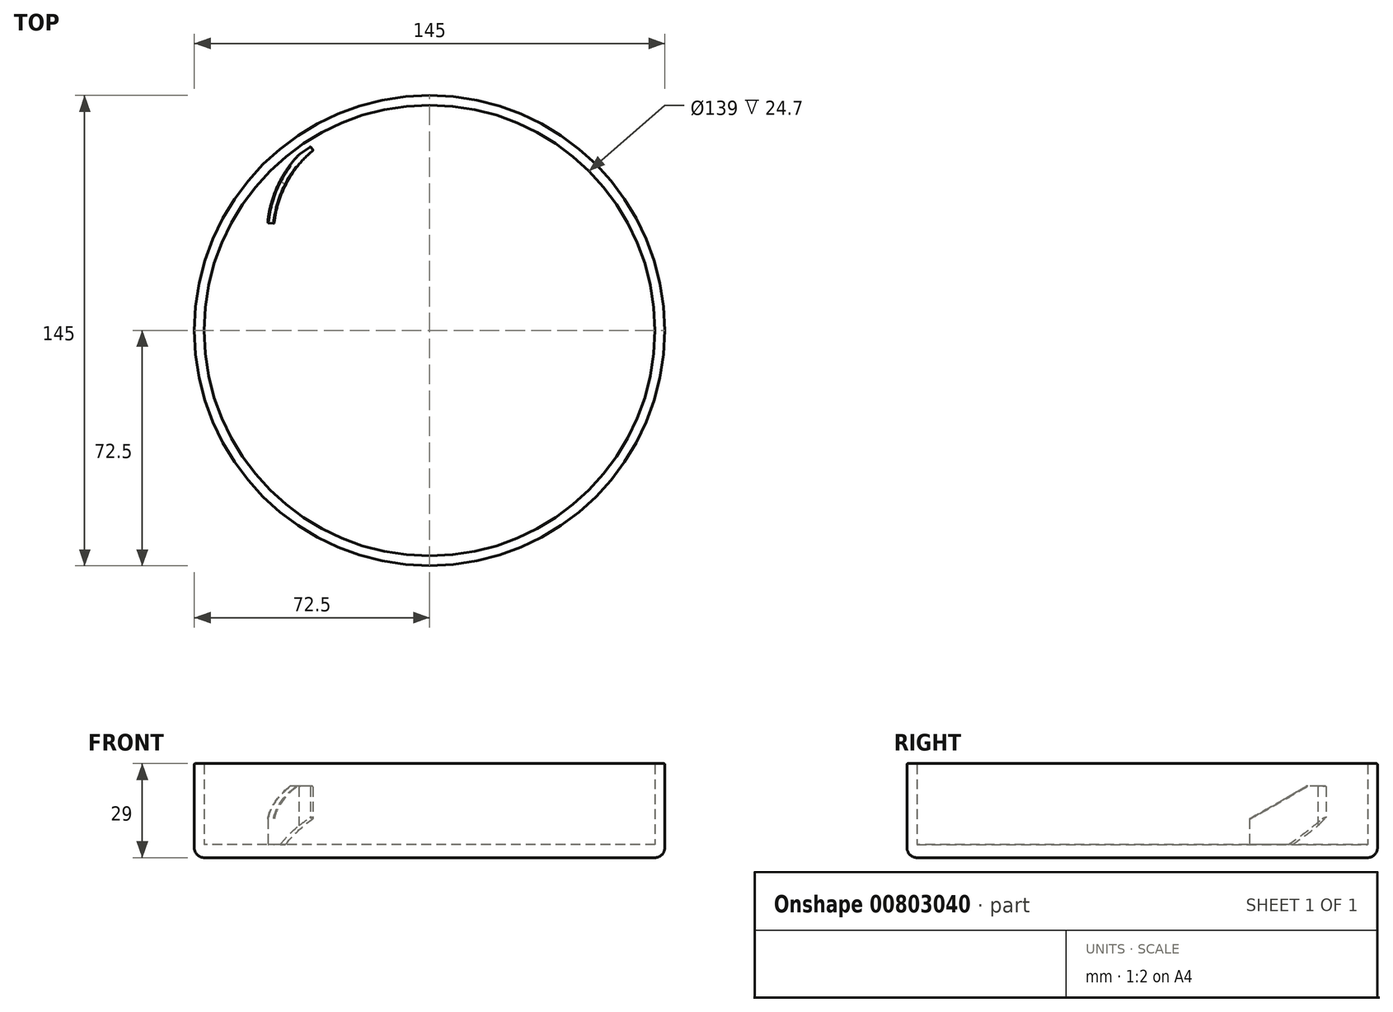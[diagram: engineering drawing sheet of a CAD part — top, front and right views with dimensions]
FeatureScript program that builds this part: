
annotation { "Feature Type Name" : "Feature", "Feature Type Description" : "" }
export const myFeature = defineFeature(function(context is Context, id is Id, definition is map)
    precondition{}
    {
        {
            var Q0;
            Q0=qCreatedBy(makeId("Top.planeOp"),FACE);
            var sketch = newSketch(context, id + "F0", { "sketchPlane" : qUnion([Q0])});
            skCircle(sketch, "E0", {"center": v(0, 0) * mm, "radius": 72.5 * mm});
            skSolve(sketch);
        }
        {
            var Q0;
            Q0 = qSketchRegion(id + "F0", true);
            extrude(context, id + "F1", {"entities" : qUnion([Q0]), "depth" : 4 * mm, "offsetDistance" : 25 * mm});
        }
        {
            var Q0;
            Q0=makeQuery(id+"F1.opExtrude","CAP_FACE",FACE,{"disambiguationData":[OSD([sQuery(id+"F0.wireOp",EDGE,"E0")])],"isStart":false});
            var sketch = newSketch(context, id + "F2", { "sketchPlane" : qUnion([Q0])});
            skCircle(sketch, "E1", {"center": v(0, 0) * mm, "radius": 69.5 * mm});
            skSolve(sketch);
        }
        {
            var Q0;
            Q0=makeQuery(id+"F2.imprint","IMPRINT",FACE,{"disambiguationData":[TD([[makeQuery(id+"F2.imprint","IMPRINT",EDGE,{"derivedFrom":sQuery(id+"F2.wireOp",EDGE,"E1")}),-1.0]])]});
            extrude(context, id + "F3", {"entities" : qUnion([Q0]), "operationType" : NewBodyOperationType.ADD, "depth" : 25 * mm, "offsetDistance" : 25 * mm});
        }
        {
            var Q0;
            Q0=makeQuery(id+"F1.opExtrude","CAP_FACE",FACE,{"disambiguationData":[OSD([sQuery(id+"F0.wireOp",EDGE,"E0")])],"isStart":false});
            var sketch = newSketch(context, id + "F4", { "sketchPlane" : qUnion([Q0])});
            skArc(sketch, "E2", {"start": v(-37.1, 57.14) * mm, "mid": v(-45.9, 46.45) * mm, "end": v(-49.86, 33.18) * mm});
            skArc(sketch, "E3", {"start": v(-35.83, 55.6) * mm, "mid": v(-44.13, 45.51) * mm, "end": v(-47.86, 33) * mm});
            skLineSegment(sketch, "E4", {"start": v(-35.83, 55.6) * mm, "end": v(-37.1, 57.14) * mm});
            skLineSegment(sketch, "E5", {"start": v(-47.86, 33) * mm, "end": v(-49.86, 33.18) * mm});
            skSolve(sketch);
        }
        {
            var Q0;
            Q0 = qSketchRegion(id + "F4", true);
            extrude(context, id + "F5", {"entities" : qUnion([Q0]), "operationType" : NewBodyOperationType.ADD, "depth" : 18 * mm, "offsetDistance" : 25 * mm});
        }
        {
            var Q0;
            Q0=qCreatedBy(makeId("Right.planeOp"),FACE);
            cPlane(context, id + "F6", {"entities" : qUnion([Q0]), "cplaneType" : CPlaneType.OFFSET, "offset" : 35 * mm, "oppositeDirection" : true, "width" : 150 * mm, "height" : 150 * mm});
        }
        {
            var Q0;
            Q0=qCreatedBy(id+"F6.planeOp",FACE);
            var sketch = newSketch(context, id + "F7", { "sketchPlane" : qUnion([Q0])});
            skLineSegment(sketch, "E6", {"start": v(57.14, 4) * mm, "end": v(42.14, 4) * mm});
            skLineSegment(sketch, "E7", {"start": v(42.14, 4) * mm, "end": v(57.14, 13) * mm});
            skLineSegment(sketch, "E8", {"start": v(57.14, 13) * mm, "end": v(57.14, 4) * mm});
            skLineSegment(sketch, "E9", {"start": v(59.14, 4) * mm, "end": v(59.14, 17.57) * mm});
            skSolve(sketch);
        }
        {
            var Q0;
            Q0=makeQuery(id+"F7.imprint","IMPRINT",FACE,{"disambiguationData":[TD([[makeQuery(id+"F7.imprint","IMPRINT",EDGE,{"derivedFrom":sQuery(id+"F7.wireOp",EDGE,"E6")}),-1.0]])]});
            var Q1;
            Q1=sQuery(id+"F7.wireOp",EDGE,"E9");
            revolve(context, id + "F8", {"operationType" : NewBodyOperationType.REMOVE, "surfaceOperationType" : NewSurfaceOperationType.NEW, "entities" : qUnion([Q0]), "axis" : qUnion([Q1]), "revolveType" : RevolveType.ONE_DIRECTION, "oppositeDirection" : true, "angle" : 50 * degree});
        }
        {
            var Q0;
            Q0=makeQuery(id+"F5.opExtrude","CAP_EDGE",EDGE,{"disambiguationData":[OSD([sQuery(id+"F4.wireOp",EDGE,"E5")])],"isStart":false});
            chamfer(context, id + "F9", {"entities" : qUnion([Q0]), "chamferType" : ChamferType.TWO_OFFSETS, "width1" : 10 * mm, "oppositeDirection" : false, "width2" : 18 * mm, "tangentPropagation" : true});
        }
        {
            var Q0;
            Q0=makeQuery(id+"F5.opExtrude","SWEPT_EDGE",EDGE,{"disambiguationData":[OSD([sQuery(id+"F4.wireOp",EDGE,"E3"),sQuery(id+"F4.wireOp",EDGE,"E5")])]});
            var Q1;
            Q1=makeQuery(id+"F5.opExtrude","SWEPT_EDGE",EDGE,{"disambiguationData":[OSD([sQuery(id+"F4.wireOp",EDGE,"E2"),sQuery(id+"F4.wireOp",EDGE,"E5")])]});
            var Q2;
            Q2=makeQuery(id+"F9.opChamfer","BLEND_FACE",FACE,{"disambiguationData":[OSD([sQuery(id+"F4.wireOp",EDGE,"E5")])]});
            var Q3;
            Q3=makeQuery(id+"F5.opExtrude","CAP_FACE",FACE,{"disambiguationData":[OSD([sQuery(id+"F4.wireOp",EDGE,"E2"),sQuery(id+"F4.wireOp",EDGE,"E3"),sQuery(id+"F4.wireOp",EDGE,"E4"),sQuery(id+"F4.wireOp",EDGE,"E5")])],"isStart":false});
            var Q4;
            Q4=makeQuery(id+"F5.opExtrude","SWEPT_EDGE",EDGE,{"disambiguationData":[OSD([sQuery(id+"F4.wireOp",EDGE,"E3"),sQuery(id+"F4.wireOp",EDGE,"E4")])]});
            var Q5;
            Q5=makeQuery(id+"F8.boolean.opBoolean","INTERSECT",EDGE,{"derivedFrom":[makeQuery(id+"F5.opExtrude","SWEPT_FACE",FACE,{"disambiguationData":[OSD([sQuery(id+"F4.wireOp",EDGE,"E4")])]}),makeQuery(id+"F8.opRevolve","SWEPT_FACE",FACE,{"disambiguationData":[OSD([sQuery(id+"F7.wireOp",EDGE,"E7")])]})]});
            var Q6;
            Q6=makeQuery(id+"F5.opExtrude","SWEPT_EDGE",EDGE,{"disambiguationData":[OSD([sQuery(id+"F4.wireOp",EDGE,"E2"),sQuery(id+"F4.wireOp",EDGE,"E4")])]});
            fillet(context, id + "F10", {"entities" : qUnion([Q0, Q1, Q2, Q3, Q4, Q5, Q6]), "radius" : 0.2 * mm, "tangentPropagation" : true, "allowEdgeOverflow" : false});
        }
        {
            var Q0;
            Q0=makeQuery(id+"F3.opExtrude","CAP_EDGE",EDGE,{"disambiguationData":[OSD([sQuery(id+"F2.wireOp",EDGE,"E1")])],"isStart":false});
            var Q1;
            Q1=makeQuery(id+"F3.opExtrude","CAP_EDGE",EDGE,{"disambiguationData":[OSD([sQuery(id+"F0.wireOp",EDGE,"E0")])],"isStart":false});
            fillet(context, id + "F11", {"entities" : qUnion([Q0, Q1]), "radius" : 0.3 * mm, "tangentPropagation" : true, "allowEdgeOverflow" : false});
        }
        {
            var Q0;
            Q0=makeQuery(id+"F1.opExtrude","CAP_FACE",FACE,{"disambiguationData":[OSD([sQuery(id+"F0.wireOp",EDGE,"E0")])],"isStart":true});
            fillet(context, id + "F12", {"entities" : qUnion([Q0]), "radius" : 3 * mm, "tangentPropagation" : true, "allowEdgeOverflow" : false});
        }
        {
            var Q0;
            Q0=qCreatedBy(makeId("Right.planeOp"),FACE);
            var sketch = newSketch(context, id + "F13", { "sketchPlane" : qUnion([Q0])});
            skLineSegment(sketch, "E10", {"start": v(0, 0) * mm, "end": v(0, 41.38) * mm});
            skSolve(sketch);
        }
        {
            var Q0;
            Q0=makeQuery(id+"F5.opExtrude","CAP_FACE",FACE,{"disambiguationData":[OSD([sQuery(id+"F4.wireOp",EDGE,"E2"),sQuery(id+"F4.wireOp",EDGE,"E3"),sQuery(id+"F4.wireOp",EDGE,"E4"),sQuery(id+"F4.wireOp",EDGE,"E5")])],"isStart":false});
            var sketch = newSketch(context, id + "F14", { "sketchPlane" : qUnion([Q0])});
            skLineSegment(sketch, "E11", {"start": v(-36.22, 57) * mm, "end": v(-42.4, 52.73) * mm});
            skLineSegment(sketch, "E12", {"start": v(-42.4, 52.73) * mm, "end": v(-37.24, 57.5) * mm});
            skLineSegment(sketch, "E13", {"start": v(-37.24, 57.5) * mm, "end": v(-36.22, 57) * mm});
            skSolve(sketch);
        }
        {
            var Q0;
            Q0 = qSketchRegion(id + "F14", true);
            extrude(context, id + "F15", {"entities" : qUnion([Q0]), "operationType" : NewBodyOperationType.REMOVE, "oppositeDirection" : true, "depth" : 15 * mm, "offsetDistance" : 25 * mm});
        }
    });
